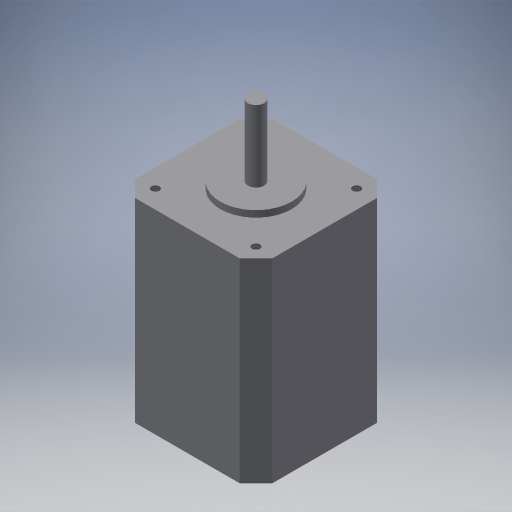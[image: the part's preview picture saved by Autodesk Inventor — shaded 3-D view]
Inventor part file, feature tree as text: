
AUTODESK INVENTOR PART (.ipt)
format: ipt  version: 2024.3 (Build 283343000, 343)  size: 262,656 bytes
history: native  units: mm
features: extrude x3, sketch x3, hole x1, chamfer x1, projected_geometry x1
ambient origin geometry x8: Origin, YZ Plane, XZ Plane, XY Plane, X Axis, Y Axis, Z Axis, Center Point
bodies: Volumenkörper1 (feature_tree)
feature tree (9):
  extrude  "Extrusion1"  Depth=42.3mm
  extrude  "Extrusion2"  Depth=22.0mm
  extrude  "Extrusion3"  Depth=2.0mm
  hole  "Bohrung1"  [1 undecoded]
  chamfer  "Fasen1"  Distance=31.0mm
  sketch  "Skizze2"  dims[d0=42.3mm d1=42.3mm]
  sketch  "Skizze3"  dims[d2=60.0mm d3=0.0mm d4=22.0mm]
  sketch  "Skizze4"  dims[d5=2.0mm d6=0.0mm d7=5.0mm d8=22.0mm d9=0.0mm d10=31.0mm d11=31.0mm d12=2.459mm d13=6.0mm d14=6.0mm d15=2.0mm d16=90.0deg d17=8.8mm d18=20.594885mm d19=5.0mm d20=2.0mm d21=45.0deg]
  projected_geometry  "Projizierte Kontur1"
note: 1 required parameter value undecoded (feature->parameter linkage not recoverable at this tier; creation-order binding heuristic only, values carry confidence <= 0.55)
